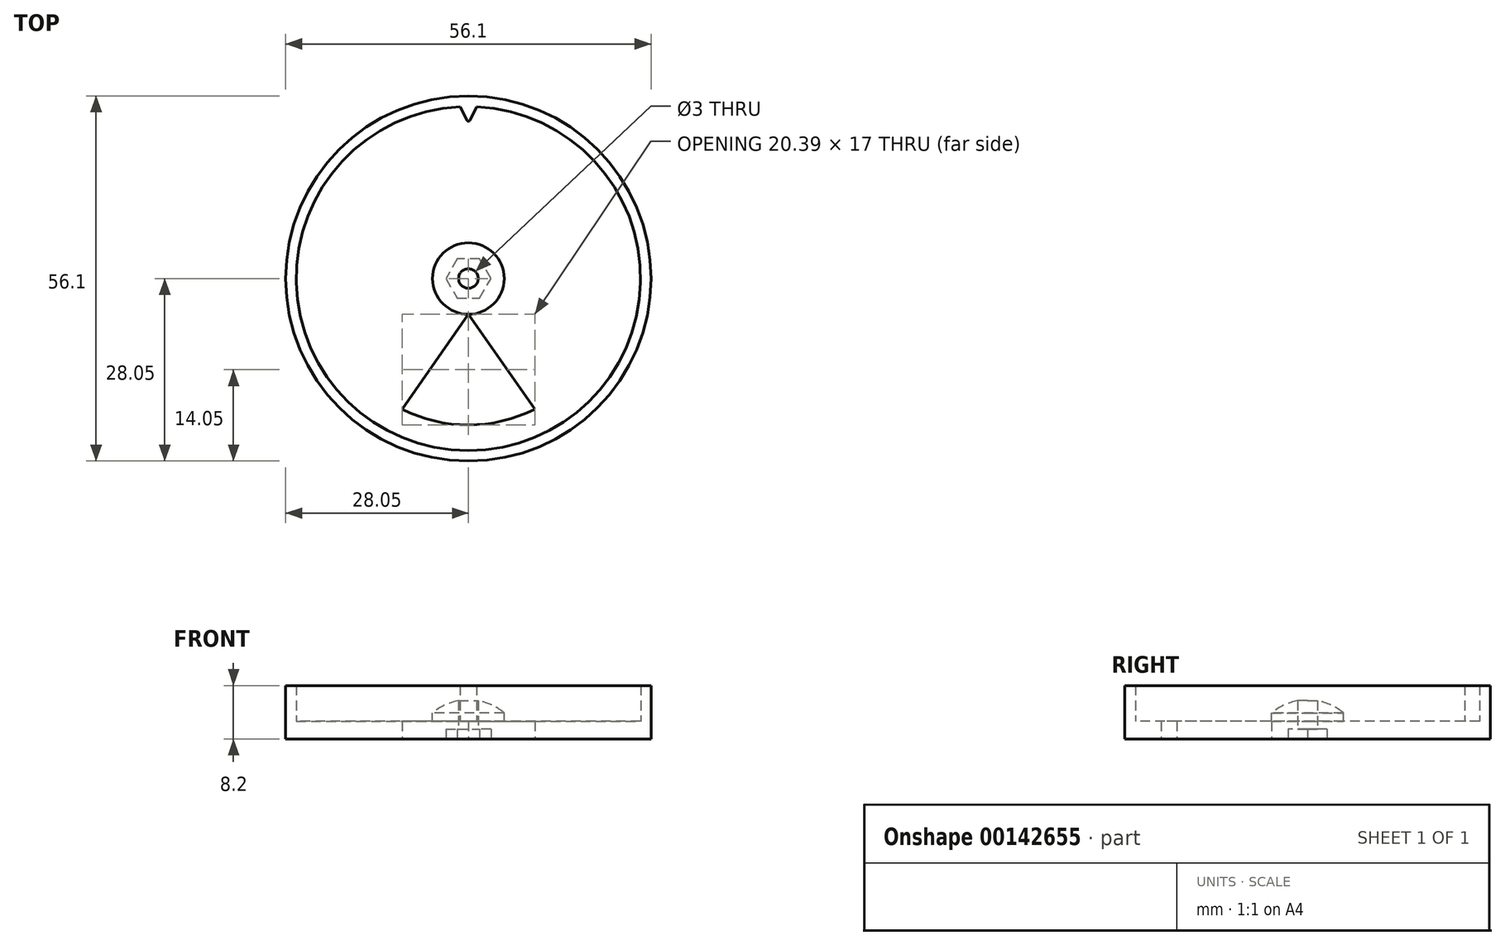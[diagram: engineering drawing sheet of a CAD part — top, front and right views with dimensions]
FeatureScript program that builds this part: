
annotation { "Feature Type Name" : "Feature", "Feature Type Description" : "" }
export const myFeature = defineFeature(function(context is Context, id is Id, definition is map)
    precondition{}
    {
        {
            var Q0;
            Q0=qCreatedBy(makeId("Top.planeOp"),FACE);
            var sketch = newSketch(context, id + "F0", { "sketchPlane" : qUnion([Q0])});
            skCircle(sketch, "E0", {"center": v(0, 0) * mm, "radius": 28.05 * mm});
            skSolve(sketch);
        }
        {
            var Q0;
            Q0=makeQuery(id+"F0.imprint","IMPRINT",FACE,{"disambiguationData":[TD([[makeQuery(id+"F0.imprint","IMPRINT",EDGE,{"derivedFrom":sQuery(id+"F0.wireOp",EDGE,"E0")}),1.0]])]});
            extrude(context, id + "F1", {"entities" : qUnion([Q0]), "depth" : 2.7 * mm});
        }
        {
            var Q0;
            Q0=makeQuery(id+"F1.opExtrude","CAP_FACE",FACE,{"disambiguationData":[OSD([sQuery(id+"F0.wireOp",EDGE,"E0")])],"isStart":false});
            var sketch = newSketch(context, id + "F2", { "sketchPlane" : qUnion([Q0])});
            skCircle(sketch, "E1", {"center": v(0, 0) * mm, "radius": 24.15 * mm, "construction": true});
            skCircle(sketch, "E2.0", {"center": v(0, 0) * mm, "radius": 26.45 * mm});
            skLineSegment(sketch, "E3", {"start": v(0, 0) * mm, "end": v(0, 28.05) * mm, "construction": true});
            skLineSegment(sketch, "E4", {"start": v(-1.26, 26.42) * mm, "end": v(0, 0) * mm, "construction": true});
            skLineSegment(sketch, "E5", {"start": v(1.26, 26.42) * mm, "end": v(0, 0) * mm, "construction": true});
            skLineSegment(sketch, "E6", {"start": v(-1.26, 26.42) * mm, "end": v(-1.3, 27.05) * mm});
            skLineSegment(sketch, "E7", {"start": v(1.26, 26.42) * mm, "end": v(1.3, 27.05) * mm});
            skLineSegment(sketch, "E8", {"start": v(-1.3, 27.05) * mm, "end": v(1.3, 27.05) * mm});
            skPoint(sketch, "E9.orphan", {"position": v(0, 24.15) * mm});
            skArc(sketch, "E10", {"start": v(-0.22, 24.3) * mm, "mid": v(0, 24.15) * mm, "end": v(0.22, 24.3) * mm});
            skLineSegment(sketch, "E11", {"start": v(-1.26, 26.42) * mm, "end": v(-0.22, 24.3) * mm});
            skLineSegment(sketch, "E12", {"start": v(1.26, 26.42) * mm, "end": v(0.22, 24.3) * mm});
            skSolve(sketch);
        }
        {
            var Q0;
            {var subQ0=sQuery(id+"F2.wireOp",EDGE,"E6");Q0=makeQuery(id+"F2.imprint","IMPRINT",FACE,{"disambiguationData":[TD([[makeQuery(id+"F2.imprint","IMPRINT",EDGE,{"derivedFrom":subQ0}),-1.0]])]});}
            var Q1;
            {var subQ0=sQuery(id+"F2.wireOp",EDGE,"wMUEv2t6-d7hM-q22d-jmSS-i0iPBbxixO15");Q1=makeQuery(id+"F2.imprint","IMPRINT",FACE,{"disambiguationData":[TD([[makeQuery(id+"F2.imprint","IMPRINT",EDGE,{"derivedFrom":subQ0}),-1.0]])]});}
            var Q2;
            Q2=makeQuery(id+"F2.imprint","IMPRINT",FACE,{"disambiguationData":[TD([[makeQuery(id+"F2.imprint","IMPRINT",EDGE,{"derivedFrom":sQuery(id+"F2.wireOp",EDGE,"E10")}),1.0]])]});
            var Q3;
            Q3 = qConstructionFilter(qBodyType(qCreatedBy(id + "F2" ,EDGE), BodyType.WIRE), ConstructionObject.NO);
            extrude(context, id + "F3", {"entities" : qUnion([Q0, Q1, Q2]), "operationType" : NewBodyOperationType.ADD, "surfaceEntities" : qUnion([Q3]), "depth" : 5.5 * mm});
        }
        {
            var Q0;
            {var subQ1=sQuery(id+"F2.wireOp",EDGE,"E6");Q0=makeQuery(id+"F2.imprint","IMPRINT",FACE,{"disambiguationData":[TD([[makeQuery(id+"F2.imprint","IMPRINT",EDGE,{"derivedFrom":subQ1}),1.0]])]});}
            var Q1;
            Q1=makeQuery(id+"F3.opExtrude","CAP_FACE",FACE,{"disambiguationData":[OSD([sQuery(id+"F2.wireOp",EDGE,"wMUEv2t6-d7hM-q22d-jmSS-i0iPBbxixO15"),sQuery(id+"F2.wireOp",EDGE,"cb6f7450-5397-4cad-ace0-c3e9583a9f1f0.MirrorCS"),sQuery(id+"F2.wireOp",EDGE,"E6"),sQuery(id+"F2.wireOp",EDGE,"E7"),sQuery(id+"F2.wireOp",EDGE,"E8")])],"isStart":false});
            extrude(context, id + "F4", {"entities" : qUnion([Q0]), "operationType" : NewBodyOperationType.ADD, "endBound" : BoundingType.UP_TO_SURFACE, "endBoundEntityFace" : qUnion([Q1]), "depth" : 25 * mm});
        }
        {
            var Q0;
            Q0=qCreatedBy(makeId("Front.planeOp"),FACE);
            var sketch = newSketch(context, id + "F5", { "sketchPlane" : qUnion([Q0])});
            skLineSegment(sketch, "E13", {"start": v(-5.5, 0) * mm, "end": v(-5.5, 4) * mm});
            skLineSegment(sketch, "E14", {"start": v(0, 6) * mm, "end": v(0, 0) * mm});
            skLineSegment(sketch, "E15", {"start": v(0, 0) * mm, "end": v(-5.5, 0) * mm});
            skLineSegment(sketch, "E16", {"start": v(0, 6) * mm, "end": v(-10, 6) * mm, "construction": true});
            skArc(sketch, "E17", {"start": v(0, 6) * mm, "mid": v(-2.93, 5.48) * mm, "end": v(-5.5, 4) * mm});
            skSolve(sketch);
        }
        {
            var Q0;
            Q0 = qSketchRegion(id + "F5", true);
            var Q1;
            Q1=sQuery(id+"F5.wireOp",EDGE,"E14");
            revolve(context, id + "F6", {"operationType" : NewBodyOperationType.ADD, "entities" : qUnion([Q0]), "axis" : qUnion([Q1]), "revolveType" : RevolveType.FULL});
        }
        {
            var Q0;
            Q0=makeQuery(id+"F1.opExtrude","CAP_FACE",FACE,{"disambiguationData":[OSD([sQuery(id+"F0.wireOp",EDGE,"E0")])],"isStart":true});
            var sketch = newSketch(context, id + "F7", { "sketchPlane" : qUnion([Q0])});
            skCircle(sketch, "E18.cCircle", {"center": v(0, 0) * mm, "radius": 3 * mm, "construction": true});
            skLineSegment(sketch, "E18.0", {"start": v(-1.73, 3) * mm, "end": v(1.73, 3) * mm});
            skLineSegment(sketch, "E18.1", {"start": v(1.73, 3) * mm, "end": v(3.46, 0) * mm});
            skLineSegment(sketch, "E18.2", {"start": v(3.46, 0) * mm, "end": v(1.73, -3) * mm});
            skLineSegment(sketch, "E18.3", {"start": v(1.73, -3) * mm, "end": v(-1.73, -3) * mm});
            skLineSegment(sketch, "E18.4", {"start": v(-1.73, -3) * mm, "end": v(-3.46, 0) * mm});
            skLineSegment(sketch, "E18.5", {"start": v(-3.46, 0) * mm, "end": v(-1.73, 3) * mm});
            skPoint(sketch, "E18.0.midPoint", {"position": v(0, 3) * mm});
            skArc(sketch, "E19", {"start": v(10.2, 20.06) * mm, "mid": v(0, 22.5) * mm, "end": v(-10.2, 20.06) * mm});
            skCircle(sketch, "E20", {"center": v(0, 0) * mm, "radius": 5.5 * mm, "construction": true});
            skLineSegment(sketch, "E21", {"start": v(0, 5.5) * mm, "end": v(-10.2, 20.06) * mm});
            skLineSegment(sketch, "E22", {"start": v(0, 0) * mm, "end": v(0, 22.5) * mm, "construction": true});
            skLineSegment(sketch, "E23.MirrorCS", {"start": v(0, 5.5) * mm, "end": v(10.2, 20.06) * mm});
            skCircle(sketch, "E24", {"center": v(0, 0) * mm, "radius": 1.5 * mm});
            skSolve(sketch);
        }
        {
            var Q0;
            Q0=makeQuery(id+"F7.imprint","IMPRINT",FACE,{"disambiguationData":[TD([[makeQuery(id+"F7.imprint","IMPRINT",EDGE,{"derivedFrom":sQuery(id+"F7.wireOp",EDGE,"E19")}),1.0]])]});
            extrude(context, id + "F8", {"entities" : qUnion([Q0]), "operationType" : NewBodyOperationType.REMOVE, "endBound" : BoundingType.UP_TO_NEXT, "oppositeDirection" : true, "depth" : 25 * mm});
        }
        {
            var Q0;
            Q0=makeQuery(id+"F7.imprint","IMPRINT",FACE,{"disambiguationData":[TD([[makeQuery(id+"F7.imprint","IMPRINT",EDGE,{"derivedFrom":sQuery(id+"F7.wireOp",EDGE,"E18.0")}),-1.0]])]});
            var Q1;
            Q1=makeQuery(id+"F7.imprint","IMPRINT",FACE,{"disambiguationData":[TD([[makeQuery(id+"F7.imprint","IMPRINT",EDGE,{"derivedFrom":sQuery(id+"F7.wireOp",EDGE,"E24")}),1.0]])]});
            extrude(context, id + "F9", {"entities" : qUnion([Q0, Q1]), "operationType" : NewBodyOperationType.REMOVE, "oppositeDirection" : true, "depth" : 1.5 * mm});
        }
        {
            var Q0;
            Q0=makeQuery(id+"F7.imprint","IMPRINT",FACE,{"disambiguationData":[TD([[makeQuery(id+"F7.imprint","IMPRINT",EDGE,{"derivedFrom":sQuery(id+"F7.wireOp",EDGE,"E24")}),1.0]])]});
            extrude(context, id + "F10", {"entities" : qUnion([Q0]), "operationType" : NewBodyOperationType.REMOVE, "endBound" : BoundingType.THROUGH_ALL, "oppositeDirection" : true, "depth" : 25 * mm});
        }
    });
